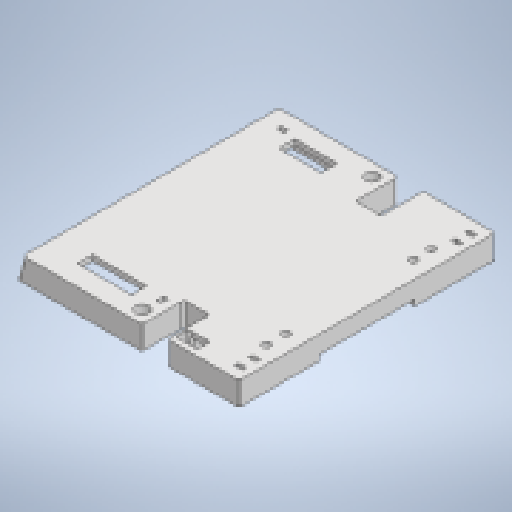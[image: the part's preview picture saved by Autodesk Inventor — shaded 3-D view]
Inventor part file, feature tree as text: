
AUTODESK INVENTOR PART (.ipt)
format: ipt  version: 2023 (Build 270158000, 158)  size: 393,728 bytes
history: native  units: mm
features: reference x36, extrude x8, sketch x8, other x5, projected_geometry x4, fillet x1
ambient origin geometry x8: Origin, YZ Plane, XZ Plane, XY Plane, X Axis, Y Axis, Z Axis, Center Point
bodies: Body1 (feature_tree)
feature tree (62):
  other  "Bryła1"
  extrude  "Wyciągnięcie proste1"  Depth=1.0mm
  extrude  "Wyciągnięcie proste2"  Depth=1.0mm
  extrude  "Wyciągnięcie proste3"  Depth=1.0mm
  extrude  "Wyciągnięcie proste4"  Depth=1.0mm
  extrude  "Wyciągnięcie proste5"  Depth=1.0mm
  extrude  "Wyciągnięcie proste6"  Depth=3.5mm TaperAngle=0.0deg
  fillet  "Zaokrąglenie1"  Radius=1.05mm
  extrude  "Wyciągnięcie proste7"  Depth=3.0mm TaperAngle=0.0deg
  extrude  "Wyciągnięcie proste8"  TaperAngle=0.0deg  [1 undecoded]
  sketch  "Szkic1"
  sketch  "Szkic2"
  projected_geometry  "Pętla rzutowana1"
  sketch  "Szkic3"
  projected_geometry  "Pętla rzutowana2"
  sketch  "Szkic4"
  reference  "Odniesienie1"
  projected_geometry  "Pętla rzutowana3"
  sketch  "Szkic5"
  reference  "Odniesienie2"
  reference  "Odniesienie3"
  reference  "Odniesienie4"
  reference  "Odniesienie5"
  reference  "Odniesienie6"
  reference  "Odniesienie7"
  reference  "Odniesienie8"
  reference  "Odniesienie9"
  reference  "Odniesienie10"
  reference  "Odniesienie11"
  reference  "Odniesienie12"
  reference  "Odniesienie13"
  reference  "Odniesienie14"
  reference  "Odniesienie15"
  reference  "Odniesienie16"
  reference  "Odniesienie17"
  reference  "Odniesienie18"
  reference  "Odniesienie19"
  reference  "Odniesienie20"
  reference  "Odniesienie21"
  sketch  "Szkic6"
  reference  "Odniesienie22"
  reference  "Odniesienie23"
  reference  "Odniesienie24"
  sketch  "Szkic7"
  projected_geometry  "Pętla rzutowana4"
  sketch  "Szkic8"
  reference  "Odniesienie25"
  reference  "Odniesienie26"
  reference  "Odniesienie27"
  reference  "Odniesienie28"
  reference  "Odniesienie29"
  reference  "Odniesienie30"
  reference  "Odniesienie31"
  reference  "Odniesienie32"
  reference  "Odniesienie33"
  reference  "Odniesienie34"
  reference  "Odniesienie35"
  reference  "Odniesienie36"
  other  "<userpath>\Documents\PROJECTS - repos\Stratos---MicroSumo\mechanics\byk_alternator.iam"
  other  "byk_alternator.iam"
  other  "noz2:1"
  other  "MikroSumo:2"
note: 1 required parameter value undecoded (feature->parameter linkage not recoverable at this tier; creation-order binding heuristic only, values carry confidence <= 0.55)
